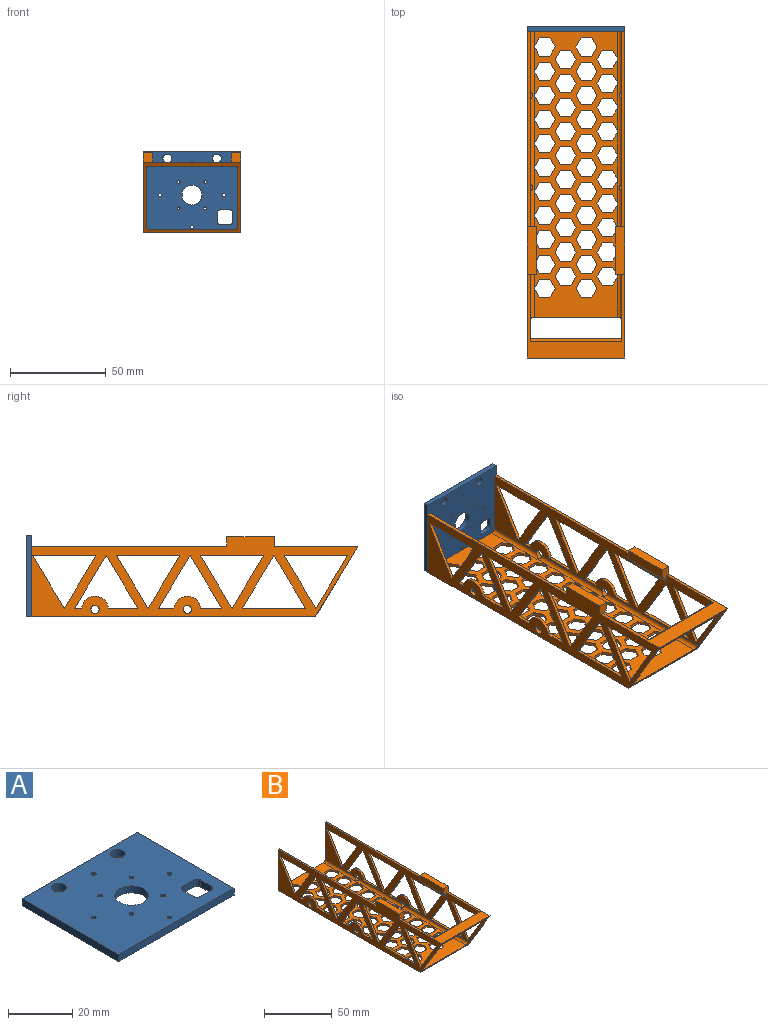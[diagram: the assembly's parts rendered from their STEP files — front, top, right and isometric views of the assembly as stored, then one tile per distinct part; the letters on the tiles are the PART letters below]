
ASSEMBLY  parts=2 mates=1
PART A: 25 faces, bbox 50.8x42.8x2.7 mm
  f0: cylinder r=1.5mm len=2.66mm, axis (0,0,-1), area 6.3mm2, adj f1,f20,f23,f24
  f1: plane 4.72x2.66mm, normal (-1,0,0), area 12.6mm2, adj f0,f2,f23,f24
  f2: cylinder r=1.5mm len=2.66mm, axis (0,0,-1), area 6.3mm2, adj f1,f3,f23,f24
  f3: plane 4.9x2.66mm, normal (0,1,0), area 13mm2, adj f2,f4,f23,f24
  f4: cylinder r=1.5mm len=2.66mm, axis (0,0,-1), area 6.3mm2, adj f3,f5,f23,f24
  f5: plane 4.72x2.66mm, normal (1,0,0), area 12.6mm2, adj f4,f6,f23,f24
  f6: cylinder r=1.5mm len=2.66mm, axis (0,0,-1), area 6.3mm2, adj f5,f20,f23,f24
  f7: plane 42.8x2.66mm, normal (1,0,0), area 113.8mm2, adj f8,f21,f23,f24
  f8: plane 50.75x2.66mm, normal (0,1,0), area 135mm2, adj f7,f9,f23,f24
  f9: plane 42.8x2.66mm, normal (-1,0,0), area 113.8mm2, adj f8,f21,f23,f24
  f10: cylinder r=0.75mm len=2.66mm, axis (0,0,-1), area 12.5mm2, adj f23,f24
  f11: cylinder r=0.75mm len=2.66mm, axis (0,0,-1), area 12.5mm2, adj f23,f24
  f12: cylinder r=0.75mm len=2.66mm, axis (0,0,-1), area 12.5mm2, adj f23,f24
  f13: cylinder r=0.75mm len=2.66mm, axis (0,0,-1), area 12.5mm2, adj f23,f24
  f14: cylinder r=0.75mm len=2.66mm, axis (0,0,-1), area 12.5mm2, adj f23,f24
  f15: cylinder r=0.75mm len=2.66mm, axis (0,0,-1), area 12.5mm2, adj f23,f24
  f16: cylinder r=0.75mm len=2.66mm, axis (0,0,-1), area 12.5mm2, adj f23,f24
  f17: cylinder r=2.3mm len=4.6mm, axis (0,0,-1), area 38.4mm2, adj f23,f24
  f18: cylinder r=2.3mm len=4.6mm, axis (0,0,-1), area 38.4mm2, adj f23,f24
  f19: cylinder r=5.22mm len=10.44mm, axis (0,0,-1), area 87.2mm2, adj f23,f24
  f20: plane 4.9x2.66mm, normal (0,-1,0), area 13mm2, adj f0,f6,f23,f24
  f21: plane 50.75x2.66mm, normal (0,-1,0), area 135mm2, adj f7,f9,f23,f24
  f22: cylinder r=0.75mm len=2.66mm, axis (0,0,-1), area 12.5mm2, adj f23,f24
  f23: plane 50.75x42.8mm, normal (0,0,1), area 1980.1mm2, adj f0,f1,f2,f3,f4,f5,f6,f7
  f24: plane 50.75x42.8mm, normal (0,0,-1), area 1980.1mm2, adj f0,f1,f2,f3,f4,f5,f6,f7
PART B: 341 faces, bbox 50.8x170.8x42 mm
  f0: plane 148.45x50.75mm, normal (0,0,-1), area 4287mm2, adj f4,f5,f14,f78,f79,f80,f81,f82
  f1: plane 149.4x43.59mm, normal (0,0,1), area 3265.6mm2, adj f6,f7,f14,f78,f79,f80,f81,f82
  f2: plane 169.25x33.42mm, normal (-1,0,0), area 2176.3mm2, adj f6,f8,f9,f14,f15,f16,f18,f21
  f3: plane 169.25x33.42mm, normal (1,0,0), area 2176.3mm2, adj f7,f8,f9,f11,f12,f13,f14,f19
  f4: plane 170.76x42mm, normal (1,0,0), area 2961.7mm2, adj f0,f8,f10,f14,f15,f16,f18,f21
  f5: plane 170.76x42mm, normal (-1,0,0), area 2961.7mm2, adj f0,f8,f11,f12,f13,f14,f17,f19
  f6: cylinder r=2mm len=150.61mm, axis (0,-1,0), area 456.7mm2, adj f1,f2,f14,f21,f22,f92,f123,f136
  f7: cylinder r=2mm len=150.61mm, axis (0,-1,0), area 456.7mm2, adj f1,f3,f14,f19,f20,f340
  f8: plane 50.75x43.72mm, normal (0,0,1), area 559.1mm2, adj f2,f3,f4,f5,f13,f18,f77,f340
  f9: plane 47.59x7.34mm, normal (0,0,-1), area 349.2mm2, adj f2,f3,f77,f340
  f10: plane 24.8x4.75mm, normal (0,0,1), area 117.8mm2, adj f4,f16,f18,f74
  f11: plane 102.24x1.58mm, normal (0,0,1), area 161.5mm2, adj f3,f5,f12,f14
  f12: plane 9.65x4.75mm, normal (0,1,0), area 27.8mm2, adj f3,f5,f11,f17,f73,f76
  f13: plane 9.65x4.75mm, normal (0,-1,0), area 27.8mm2, adj f3,f5,f8,f17,f73,f76
  f14: plane 50.75x37mm, normal (0,1,0), area 193.8mm2, adj f0,f1,f2,f3,f4,f5,f6,f7
  f15: plane 102.24x1.58mm, normal (0,0,1), area 161.5mm2, adj f2,f4,f14,f16
  f16: plane 9.65x4.75mm, normal (0,1,0), area 27.8mm2, adj f2,f4,f10,f15,f74,f75
  f17: plane 24.8x4.75mm, normal (0,0,1), area 117.8mm2, adj f5,f12,f13,f73
  f18: plane 9.65x4.75mm, normal (0,-1,0), area 27.8mm2, adj f2,f4,f8,f10,f74,f75
  f19: cylinder r=2.15mm len=4.3mm, axis (-1,0,0), area 24.8mm2, adj f3,f5,f7
  f20: cylinder r=2.15mm len=4.3mm, axis (-1,0,0), area 24.8mm2, adj f3,f5,f7
  f21: cylinder r=2.15mm len=4.3mm, axis (-1,0,0), area 24.8mm2, adj f2,f4,f6
  f22: cylinder r=2.15mm len=4.3mm, axis (-1,0,0), area 24.8mm2, adj f2,f4,f6
  f23: plane 27.42x16.53mm, normal (0,-0.86,0.52), area 50.6mm2, adj f2,f4,f24,f25
  f24: plane 27.42x16.53mm, normal (0,0.86,0.52), area 50.6mm2, adj f2,f4,f23,f25
  f25: plane 33.06x1.58mm, normal (0,0,-1), area 52.2mm2, adj f2,f4,f23,f24
  f26: plane 27.42x16.53mm, normal (0,-0.86,0.52), area 50.6mm2, adj f2,f4,f27,f28
  f27: plane 27.42x16.53mm, normal (0,0.86,0.52), area 50.6mm2, adj f2,f4,f26,f28
  f28: plane 33.06x1.58mm, normal (0,0,-1), area 52.2mm2, adj f2,f4,f26,f27
  f29: plane 11.02x1.58mm, normal (0,0,1), area 17.4mm2, adj f2,f4,f30,f33
  f30: plane 27.42x16.53mm, normal (0,0.86,-0.52), area 50.6mm2, adj f2,f4,f29,f31
  f31: plane 27.42x16.53mm, normal (0,-0.86,-0.52), area 50.6mm2, adj f2,f4,f30,f32
  f32: plane 8.11x1.58mm, normal (0,0,1), area 12.8mm2, adj f2,f4,f31,f33
  f33: cylinder r=7mm len=13.93mm, axis (-1,0,0), area 32.5mm2, adj f2,f4,f29,f32
  f34: plane 27.42x16.53mm, normal (0,0.86,-0.52), area 50.6mm2, adj f2,f4,f35,f38
  f35: plane 27.42x16.53mm, normal (0,-0.86,-0.52), area 50.6mm2, adj f2,f4,f34,f36
  f36: plane 3.72x1.58mm, normal (0,0,1), area 5.9mm2, adj f2,f4,f35,f37
  f37: cylinder r=7mm len=13.93mm, axis (-1,0,0), area 32.5mm2, adj f2,f4,f36,f38
  f38: plane 15.41x1.58mm, normal (0,0,1), area 24.4mm2, adj f2,f4,f34,f37
  f39: plane 33.06x1.58mm, normal (0,0,1), area 52.2mm2, adj f2,f4,f40,f41
  f40: plane 27.42x16.53mm, normal (0,0.86,-0.52), area 50.6mm2, adj f2,f4,f39,f41
  f41: plane 27.42x16.53mm, normal (0,-0.86,-0.52), area 50.6mm2, adj f2,f4,f39,f40
  f42: plane 27.42x16.53mm, normal (0,-0.86,0.52), area 50.6mm2, adj f2,f4,f43,f44
  f43: plane 27.42x16.53mm, normal (0,0.86,0.52), area 50.6mm2, adj f2,f4,f42,f44
  f44: plane 33.06x1.58mm, normal (0,0,-1), area 52.2mm2, adj f2,f4,f42,f43
  f45: plane 27.42x16.53mm, normal (0,-0.86,0.52), area 50.6mm2, adj f2,f4,f46,f47
  f46: plane 27.42x16.53mm, normal (0,0.86,0.52), area 50.6mm2, adj f2,f4,f45,f47
  f47: plane 33.06x1.58mm, normal (0,0,-1), area 52.2mm2, adj f2,f4,f45,f46
  f48: plane 33.06x1.58mm, normal (0,0,-1), area 52.2mm2, adj f3,f5,f49,f50
  f49: plane 27.42x16.53mm, normal (0,0.86,0.52), area 50.6mm2, adj f3,f5,f48,f50
  f50: plane 27.42x16.53mm, normal (0,-0.86,0.52), area 50.6mm2, adj f3,f5,f48,f49
  f51: plane 33.06x1.58mm, normal (0,0,-1), area 52.2mm2, adj f3,f5,f52,f53
  f52: plane 27.42x16.53mm, normal (0,0.86,0.52), area 50.6mm2, adj f3,f5,f51,f53
  f53: plane 27.42x16.53mm, normal (0,-0.86,0.52), area 50.6mm2, adj f3,f5,f51,f52
  f54: cylinder r=7mm len=13.93mm, axis (-1,0,0), area 32.5mm2, adj f3,f5,f55,f58
  f55: plane 8.11x1.58mm, normal (0,0,1), area 12.8mm2, adj f3,f5,f54,f56
  f56: plane 27.42x16.53mm, normal (0,-0.86,-0.52), area 50.6mm2, adj f3,f5,f55,f57
  f57: plane 27.42x16.53mm, normal (0,0.86,-0.52), area 50.6mm2, adj f3,f5,f56,f58
  f58: plane 11.02x1.58mm, normal (0,0,1), area 17.4mm2, adj f3,f5,f54,f57
  f59: plane 15.41x1.58mm, normal (0,0,1), area 24.4mm2, adj f3,f5,f60,f63
  f60: cylinder r=7mm len=13.93mm, axis (-1,0,0), area 32.5mm2, adj f3,f5,f59,f61
  f61: plane 3.72x1.58mm, normal (0,0,1), area 5.9mm2, adj f3,f5,f60,f62
  f62: plane 27.42x16.53mm, normal (0,-0.86,-0.52), area 50.6mm2, adj f3,f5,f61,f63
  f63: plane 27.42x16.53mm, normal (0,0.86,-0.52), area 50.6mm2, adj f3,f5,f59,f62
  f64: plane 27.42x16.53mm, normal (0,-0.86,-0.52), area 50.6mm2, adj f3,f5,f65,f66
  f65: plane 27.42x16.53mm, normal (0,0.86,-0.52), area 50.6mm2, adj f3,f5,f64,f66
  f66: plane 33.06x1.58mm, normal (0,0,1), area 52.2mm2, adj f3,f5,f64,f65
  f67: plane 33.06x1.58mm, normal (0,0,-1), area 52.2mm2, adj f3,f5,f68,f69
  f68: plane 27.42x16.53mm, normal (0,0.86,0.52), area 50.6mm2, adj f3,f5,f67,f69
  f69: plane 27.42x16.53mm, normal (0,-0.86,0.52), area 50.6mm2, adj f3,f5,f67,f68
  f70: plane 33.06x1.58mm, normal (0,0,-1), area 52.2mm2, adj f3,f5,f71,f72
  f71: plane 27.42x16.53mm, normal (0,0.86,0.52), area 50.6mm2, adj f3,f5,f70,f72
  f72: plane 27.42x16.53mm, normal (0,-0.86,0.52), area 50.6mm2, adj f3,f5,f70,f71
  f73: plane 24.8x5mm, normal (1,0,0), area 124mm2, adj f12,f13,f17,f76
  f74: plane 24.8x5mm, normal (-1,0,0), area 124mm2, adj f10,f16,f18,f75
  f75: cylinder r=5mm len=24.8mm, axis (0,-1,0), area 148.3mm2, adj f2,f16,f18,f74
  f76: cylinder r=5mm len=24.8mm, axis (0,1,0), area 148.3mm2, adj f3,f12,f13,f73
  f77: cylinder r=1.25mm len=47.59mm, axis (1,0,0), area 186.9mm2, adj f2,f3,f8,f9
  f78: plane 4.72x2.73mm, normal (0.87,-0.5,0), area 8.6mm2, adj f0,f1,f79,f82
  f79: plane 4.72x2.73mm, normal (0.87,0.5,0), area 8.6mm2, adj f0,f1,f78,f83
  f80: plane 4.72x2.73mm, normal (-0.87,0.5,0), area 8.6mm2, adj f0,f1,f81,f83
  f81: plane 4.72x2.73mm, normal (-0.87,-0.5,0), area 8.6mm2, adj f0,f1,f80,f82
  f82: plane 5.46x1.58mm, normal (0,-1,0), area 8.6mm2, adj f0,f1,f78,f81
  f83: plane 5.46x1.58mm, normal (0,1,0), area 8.6mm2, adj f0,f1,f79,f80
  f84: plane 4.72x2.73mm, normal (0.87,-0.5,0), area 8.6mm2, adj f0,f1,f85,f89
  f85: plane 4.72x2.73mm, normal (0.87,0.5,0), area 8.6mm2, adj f0,f1,f84,f86
  f86: plane 5.46x1.58mm, normal (0,1,0), area 8.6mm2, adj f0,f1,f85,f87
  f87: plane 4.72x2.73mm, normal (-0.87,0.5,0), area 8.6mm2, adj f0,f1,f86,f88
  f88: plane 4.72x2.73mm, normal (-0.87,-0.5,0), area 8.6mm2, adj f0,f1,f87,f89
  f89: plane 5.46x1.58mm, normal (0,-1,0), area 8.6mm2, adj f0,f1,f84,f88
  f90: plane 4.63x2.67mm, normal (-0.87,-0.5,0), area 8.4mm2, adj f0,f1,f92,f93
  f91: plane 4.63x2.67mm, normal (-0.87,0.5,0), area 8.4mm2, adj f0,f1,f92,f96
  f92: plane 1.58x0.19mm, normal (-1,0,0), area 0.3mm2, adj f0,f6,f90,f91
  f93: plane 5.46x1.58mm, normal (0,-1,0), area 8.6mm2, adj f0,f1,f90,f94
  f94: plane 4.72x2.73mm, normal (0.87,-0.5,0), area 8.6mm2, adj f0,f1,f93,f95
  f95: plane 4.72x2.73mm, normal (0.87,0.5,0), area 8.6mm2, adj f0,f1,f94,f96
  f96: plane 5.46x1.58mm, normal (0,1,0), area 8.6mm2, adj f0,f1,f91,f95
  f97: plane 5.46x1.58mm, normal (0,1,0), area 8.6mm2, adj f0,f1,f98,f102
  f98: plane 4.72x2.73mm, normal (-0.87,0.5,0), area 8.6mm2, adj f0,f1,f97,f99
  f99: plane 4.72x2.73mm, normal (-0.87,-0.5,0), area 8.6mm2, adj f0,f1,f98,f100
  f100: plane 5.46x1.58mm, normal (0,-1,0), area 8.6mm2, adj f0,f1,f99,f101
  f101: plane 4.72x2.73mm, normal (0.87,-0.5,0), area 8.6mm2, adj f0,f1,f100,f102
  f102: plane 4.72x2.73mm, normal (0.87,0.5,0), area 8.6mm2, adj f0,f1,f97,f101
  f103: plane 4.72x2.73mm, normal (-0.87,0.5,0), area 8.6mm2, adj f0,f1,f104,f108
  f104: plane 4.72x2.73mm, normal (-0.87,-0.5,0), area 8.6mm2, adj f0,f1,f103,f105
  f105: plane 5.46x1.58mm, normal (0,-1,0), area 8.6mm2, adj f0,f1,f104,f106
  f106: plane 4.72x2.73mm, normal (0.87,-0.5,0), area 8.6mm2, adj f0,f1,f105,f107
  f107: plane 4.72x2.73mm, normal (0.87,0.5,0), area 8.6mm2, adj f0,f1,f106,f108
  f108: plane 5.46x1.58mm, normal (0,1,0), area 8.6mm2, adj f0,f1,f103,f107
  f109: plane 4.72x2.73mm, normal (-0.87,0.5,0), area 8.6mm2, adj f0,f1,f110,f114
  f110: plane 4.72x2.73mm, normal (-0.87,-0.5,0), area 8.6mm2, adj f0,f1,f109,f111
  f111: plane 5.46x1.58mm, normal (0,-1,0), area 8.6mm2, adj f0,f1,f110,f112
  f112: plane 4.72x2.73mm, normal (0.87,-0.5,0), area 8.6mm2, adj f0,f1,f111,f113
  f113: plane 4.72x2.73mm, normal (0.87,0.5,0), area 8.6mm2, adj f0,f1,f112,f114
  f114: plane 5.46x1.58mm, normal (0,1,0), area 8.6mm2, adj f0,f1,f109,f113
  f115: plane 5.46x1.58mm, normal (0,1,0), area 8.6mm2, adj f0,f1,f116,f120
  f116: plane 4.72x2.73mm, normal (-0.87,0.5,0), area 8.6mm2, adj f0,f1,f115,f117
  f117: plane 4.72x2.73mm, normal (-0.87,-0.5,0), area 8.6mm2, adj f0,f1,f116,f118
  f118: plane 5.46x1.58mm, normal (0,-1,0), area 8.6mm2, adj f0,f1,f117,f119
  f119: plane 4.72x2.73mm, normal (0.87,-0.5,0), area 8.6mm2, adj f0,f1,f118,f120
  f120: plane 4.72x2.73mm, normal (0.87,0.5,0), area 8.6mm2, adj f0,f1,f115,f119
  f121: plane 4.63x2.68mm, normal (-0.87,-0.5,0), area 8.5mm2, adj f0,f1,f123,f124
  f122: plane 4.63x2.68mm, normal (-0.87,0.5,0), area 8.5mm2, adj f0,f1,f123,f127
  f123: plane 1.58x0.18mm, normal (-1,0,0), area 0.3mm2, adj f0,f6,f121,f122
  f124: plane 5.46x1.58mm, normal (0,-1,0), area 8.6mm2, adj f0,f1,f121,f125
  f125: plane 4.72x2.73mm, normal (0.87,-0.5,0), area 8.6mm2, adj f0,f1,f124,f126
  f126: plane 4.72x2.73mm, normal (0.87,0.5,0), area 8.6mm2, adj f0,f1,f125,f127
  f127: plane 5.46x1.58mm, normal (0,1,0), area 8.6mm2, adj f0,f1,f122,f126
  f128: plane 4.72x2.73mm, normal (0.87,-0.5,0), area 8.6mm2, adj f0,f1,f129,f133
  f129: plane 4.72x2.73mm, normal (0.87,0.5,0), area 8.6mm2, adj f0,f1,f128,f130
  f130: plane 5.46x1.58mm, normal (0,1,0), area 8.6mm2, adj f0,f1,f129,f131
  f131: plane 4.72x2.73mm, normal (-0.87,0.5,0), area 8.6mm2, adj f0,f1,f130,f132
  f132: plane 4.72x2.73mm, normal (-0.87,-0.5,0), area 8.6mm2, adj f0,f1,f131,f133
  f133: plane 5.46x1.58mm, normal (0,-1,0), area 8.6mm2, adj f0,f1,f128,f132
  f134: plane 4.63x2.67mm, normal (-0.87,-0.5,0), area 8.4mm2, adj f0,f1,f136,f137
  f135: plane 4.63x2.67mm, normal (-0.87,0.5,0), area 8.4mm2, adj f0,f1,f136,f140
  f136: plane 1.58x0.2mm, normal (-1,0,0), area 0.3mm2, adj f0,f6,f134,f135
  f137: plane 5.46x1.58mm, normal (0,-1,0), area 8.6mm2, adj f0,f1,f134,f138
  f138: plane 4.72x2.73mm, normal (0.87,-0.5,0), area 8.6mm2, adj f0,f1,f137,f139
  f139: plane 4.72x2.73mm, normal (0.87,0.5,0), area 8.6mm2, adj f0,f1,f138,f140
  f140: plane 5.46x1.58mm, normal (0,1,0), area 8.6mm2, adj f0,f1,f135,f139
  f141: plane 4.72x2.73mm, normal (0.87,-0.5,0), area 8.6mm2, adj f0,f1,f142,f146
  f142: plane 4.72x2.73mm, normal (0.87,0.5,0), area 8.6mm2, adj f0,f1,f141,f143
  f143: plane 5.46x1.58mm, normal (0,1,0), area 8.6mm2, adj f0,f1,f142,f144
  f144: plane 4.72x2.73mm, normal (-0.87,0.5,0), area 8.6mm2, adj f0,f1,f143,f145
  f145: plane 4.72x2.73mm, normal (-0.87,-0.5,0), area 8.6mm2, adj f0,f1,f144,f146
  f146: plane 5.46x1.58mm, normal (0,-1,0), area 8.6mm2, adj f0,f1,f141,f145
  f147: plane 4.62x2.67mm, normal (-0.87,-0.5,0), area 8.4mm2, adj f0,f1,f149,f150
  f148: plane 4.62x2.67mm, normal (-0.87,0.5,0), area 8.4mm2, adj f0,f1,f149,f153
  f149: plane 1.58x0.21mm, normal (-1,0,0), area 0.3mm2, adj f0,f6,f147,f148
  f150: plane 5.46x1.58mm, normal (0,-1,0), area 8.6mm2, adj f0,f1,f147,f151
  f151: plane 4.72x2.73mm, normal (0.87,-0.5,0), area 8.6mm2, adj f0,f1,f150,f152
  f152: plane 4.72x2.73mm, normal (0.87,0.5,0), area 8.6mm2, adj f0,f1,f151,f153
  f153: plane 5.46x1.58mm, normal (0,1,0), area 8.6mm2, adj f0,f1,f148,f152
  f154: plane 4.62x2.67mm, normal (-0.87,-0.5,0), area 8.4mm2, adj f0,f1,f156,f157
  f155: plane 4.62x2.67mm, normal (-0.87,0.5,0), area 8.4mm2, adj f0,f1,f156,f160
  f156: plane 1.58x0.22mm, normal (-1,0,0), area 0.3mm2, adj f0,f6,f154,f155
  f157: plane 5.46x1.58mm, normal (0,-1,0), area 8.6mm2, adj f0,f1,f154,f158
  f158: plane 4.72x2.73mm, normal (0.87,-0.5,0), area 8.6mm2, adj f0,f1,f157,f159
  f159: plane 4.72x2.73mm, normal (0.87,0.5,0), area 8.6mm2, adj f0,f1,f158,f160
  f160: plane 5.46x1.58mm, normal (0,1,0), area 8.6mm2, adj f0,f1,f155,f159
  f161: plane 4.72x2.73mm, normal (-0.87,0.5,0), area 8.6mm2, adj f0,f1,f162,f166
  f162: plane 4.72x2.73mm, normal (-0.87,-0.5,0), area 8.6mm2, adj f0,f1,f161,f163
  f163: plane 5.46x1.58mm, normal (0,-1,0), area 8.6mm2, adj f0,f1,f162,f164
  f164: plane 4.72x2.73mm, normal (0.87,-0.5,0), area 8.6mm2, adj f0,f1,f163,f165
  f165: plane 4.72x2.73mm, normal (0.87,0.5,0), area 8.6mm2, adj f0,f1,f164,f166
  f166: plane 5.46x1.58mm, normal (0,1,0), area 8.6mm2, adj f0,f1,f161,f165
  f167: plane 5.46x1.58mm, normal (0,1,0), area 8.6mm2, adj f0,f1,f168,f172
  f168: plane 4.72x2.73mm, normal (-0.87,0.5,0), area 8.6mm2, adj f0,f1,f167,f169
  f169: plane 4.72x2.73mm, normal (-0.87,-0.5,0), area 8.6mm2, adj f0,f1,f168,f170
  f170: plane 5.46x1.58mm, normal (0,-1,0), area 8.6mm2, adj f0,f1,f169,f171
  f171: plane 4.72x2.73mm, normal (0.87,-0.5,0), area 8.6mm2, adj f0,f1,f170,f172
  f172: plane 4.72x2.73mm, normal (0.87,0.5,0), area 8.6mm2, adj f0,f1,f167,f171
  f173: plane 4.72x2.73mm, normal (-0.87,0.5,0), area 8.6mm2, adj f0,f1,f174,f178
  f174: plane 4.72x2.73mm, normal (-0.87,-0.5,0), area 8.6mm2, adj f0,f1,f173,f175
  f175: plane 5.46x1.58mm, normal (0,-1,0), area 8.6mm2, adj f0,f1,f174,f176
  f176: plane 4.72x2.73mm, normal (0.87,-0.5,0), area 8.6mm2, adj f0,f1,f175,f177
  f177: plane 4.72x2.73mm, normal (0.87,0.5,0), area 8.6mm2, adj f0,f1,f176,f178
  f178: plane 5.46x1.58mm, normal (0,1,0), area 8.6mm2, adj f0,f1,f173,f177
  f179: plane 5.46x1.58mm, normal (0,1,0), area 8.6mm2, adj f0,f1,f180,f184
  f180: plane 4.72x2.73mm, normal (-0.87,0.5,0), area 8.6mm2, adj f0,f1,f179,f181
  f181: plane 4.72x2.73mm, normal (-0.87,-0.5,0), area 8.6mm2, adj f0,f1,f180,f182
  f182: plane 5.46x1.58mm, normal (0,-1,0), area 8.6mm2, adj f0,f1,f181,f183
  f183: plane 4.72x2.73mm, normal (0.87,-0.5,0), area 8.6mm2, adj f0,f1,f182,f184
  f184: plane 4.72x2.73mm, normal (0.87,0.5,0), area 8.6mm2, adj f0,f1,f179,f183
  f185: plane 5.46x1.58mm, normal (0,1,0), area 8.6mm2, adj f0,f1,f186,f190
  f186: plane 4.72x2.73mm, normal (-0.87,0.5,0), area 8.6mm2, adj f0,f1,f185,f187
  f187: plane 4.72x2.73mm, normal (-0.87,-0.5,0), area 8.6mm2, adj f0,f1,f186,f188
  f188: plane 5.46x1.58mm, normal (0,-1,0), area 8.6mm2, adj f0,f1,f187,f189
  f189: plane 4.72x2.73mm, normal (0.87,-0.5,0), area 8.6mm2, adj f0,f1,f188,f190
  f190: plane 4.72x2.73mm, normal (0.87,0.5,0), area 8.6mm2, adj f0,f1,f185,f189
  f191: plane 5.46x1.58mm, normal (0,1,0), area 8.6mm2, adj f0,f1,f192,f196
  f192: plane 4.72x2.73mm, normal (-0.87,0.5,0), area 8.6mm2, adj f0,f1,f191,f193
  f193: plane 4.72x2.73mm, normal (-0.87,-0.5,0), area 8.6mm2, adj f0,f1,f192,f194
  f194: plane 5.46x1.58mm, normal (0,-1,0), area 8.6mm2, adj f0,f1,f193,f195
  f195: plane 4.72x2.73mm, normal (0.87,-0.5,0), area 8.6mm2, adj f0,f1,f194,f196
  f196: plane 4.72x2.73mm, normal (0.87,0.5,0), area 8.6mm2, adj f0,f1,f191,f195
  f197: plane 4.72x2.73mm, normal (0.87,-0.5,0), area 8.6mm2, adj f0,f1,f198,f202
  f198: plane 4.72x2.73mm, normal (0.87,0.5,0), area 8.6mm2, adj f0,f1,f197,f199
  f199: plane 5.46x1.58mm, normal (0,1,0), area 8.6mm2, adj f0,f1,f198,f200
  f200: plane 4.72x2.73mm, normal (-0.87,0.5,0), area 8.6mm2, adj f0,f1,f199,f201
  f201: plane 4.72x2.73mm, normal (-0.87,-0.5,0), area 8.6mm2, adj f0,f1,f200,f202
  f202: plane 5.46x1.58mm, normal (0,-1,0), area 8.6mm2, adj f0,f1,f197,f201
  f203: plane 4.72x2.73mm, normal (-0.87,0.5,0), area 8.6mm2, adj f0,f1,f204,f208
  f204: plane 4.72x2.73mm, normal (-0.87,-0.5,0), area 8.6mm2, adj f0,f1,f203,f205
  f205: plane 5.46x1.58mm, normal (0,-1,0), area 8.6mm2, adj f0,f1,f204,f206
  f206: plane 4.72x2.73mm, normal (0.87,-0.5,0), area 8.6mm2, adj f0,f1,f205,f207
  f207: plane 4.72x2.73mm, normal (0.87,0.5,0), area 8.6mm2, adj f0,f1,f206,f208
  f208: plane 5.46x1.58mm, normal (0,1,0), area 8.6mm2, adj f0,f1,f203,f207
  f209: plane 5.46x1.58mm, normal (0,-1,0), area 8.6mm2, adj f0,f1,f210,f214
  f210: plane 4.72x2.73mm, normal (0.87,-0.5,0), area 8.6mm2, adj f0,f1,f209,f211
  f211: plane 4.72x2.73mm, normal (0.87,0.5,0), area 8.6mm2, adj f0,f1,f210,f212
  f212: plane 5.46x1.58mm, normal (0,1,0), area 8.6mm2, adj f0,f1,f211,f213
  f213: plane 4.72x2.73mm, normal (-0.87,0.5,0), area 8.6mm2, adj f0,f1,f212,f214
  f214: plane 4.72x2.73mm, normal (-0.87,-0.5,0), area 8.6mm2, adj f0,f1,f209,f213
  f215: plane 5.46x1.58mm, normal (0,1,0), area 8.6mm2, adj f0,f1,f216,f220
  f216: plane 4.72x2.73mm, normal (-0.87,0.5,0), area 8.6mm2, adj f0,f1,f215,f217
  f217: plane 4.72x2.73mm, normal (-0.87,-0.5,0), area 8.6mm2, adj f0,f1,f216,f218
  f218: plane 5.46x1.58mm, normal (0,-1,0), area 8.6mm2, adj f0,f1,f217,f219
  f219: plane 4.72x2.73mm, normal (0.87,-0.5,0), area 8.6mm2, adj f0,f1,f218,f220
  f220: plane 4.72x2.73mm, normal (0.87,0.5,0), area 8.6mm2, adj f0,f1,f215,f219
  f221: plane 4.69x2.71mm, normal (-0.87,-0.5,0), area 8.6mm2, adj f0,f1,f223,f224
  f222: plane 4.69x2.71mm, normal (-0.87,0.5,0), area 8.6mm2, adj f0,f1,f223,f227
  f223: plane 1.58x0.07mm, normal (-1,0,0), area 0.1mm2, adj f0,f6,f221,f222
  f224: plane 5.46x1.58mm, normal (0,-1,0), area 8.6mm2, adj f0,f1,f221,f225
  f225: plane 4.72x2.73mm, normal (0.87,-0.5,0), area 8.6mm2, adj f0,f1,f224,f226
  f226: plane 4.72x2.73mm, normal (0.87,0.5,0), area 8.6mm2, adj f0,f1,f225,f227
  f227: plane 5.46x1.58mm, normal (0,1,0), area 8.6mm2, adj f0,f1,f222,f226
  f228: plane 4.72x2.73mm, normal (-0.87,0.5,0), area 8.6mm2, adj f0,f1,f229,f233
  f229: plane 4.72x2.73mm, normal (-0.87,-0.5,0), area 8.6mm2, adj f0,f1,f228,f230
  f230: plane 5.46x1.58mm, normal (0,-1,0), area 8.6mm2, adj f0,f1,f229,f231
  f231: plane 4.72x2.73mm, normal (0.87,-0.5,0), area 8.6mm2, adj f0,f1,f230,f232
  f232: plane 4.72x2.73mm, normal (0.87,0.5,0), area 8.6mm2, adj f0,f1,f231,f233
  f233: plane 5.46x1.58mm, normal (0,1,0), area 8.6mm2, adj f0,f1,f228,f232
  f234: plane 4.72x2.73mm, normal (0.87,-0.5,0), area 8.6mm2, adj f0,f1,f235,f239
  f235: plane 4.72x2.73mm, normal (0.87,0.5,0), area 8.6mm2, adj f0,f1,f234,f236
  f236: plane 5.46x1.58mm, normal (0,1,0), area 8.6mm2, adj f0,f1,f235,f237
  f237: plane 4.72x2.73mm, normal (-0.87,0.5,0), area 8.6mm2, adj f0,f1,f236,f238
  f238: plane 4.72x2.73mm, normal (-0.87,-0.5,0), area 8.6mm2, adj f0,f1,f237,f239
  f239: plane 5.46x1.58mm, normal (0,-1,0), area 8.6mm2, adj f0,f1,f234,f238
  f240: plane 4.64x2.68mm, normal (-0.87,-0.5,0), area 8.5mm2, adj f0,f1,f242,f243
  f241: plane 4.64x2.68mm, normal (-0.87,0.5,0), area 8.5mm2, adj f0,f1,f242,f246
  f242: plane 1.58x0.17mm, normal (-1,0,0), area 0.3mm2, adj f0,f6,f240,f241
  f243: plane 5.46x1.58mm, normal (0,-1,0), area 8.6mm2, adj f0,f1,f240,f244
  f244: plane 4.72x2.73mm, normal (0.87,-0.5,0), area 8.6mm2, adj f0,f1,f243,f245
  f245: plane 4.72x2.73mm, normal (0.87,0.5,0), area 8.6mm2, adj f0,f1,f244,f246
  f246: plane 5.46x1.58mm, normal (0,1,0), area 8.6mm2, adj f0,f1,f241,f245
  f247: plane 5.46x1.58mm, normal (0,1,0), area 8.6mm2, adj f0,f1,f248,f252
  f248: plane 4.72x2.73mm, normal (-0.87,0.5,0), area 8.6mm2, adj f0,f1,f247,f249
  f249: plane 4.72x2.73mm, normal (-0.87,-0.5,0), area 8.6mm2, adj f0,f1,f248,f250
  f250: plane 5.46x1.58mm, normal (0,-1,0), area 8.6mm2, adj f0,f1,f249,f251
  f251: plane 4.72x2.73mm, normal (0.87,-0.5,0), area 8.6mm2, adj f0,f1,f250,f252
  f252: plane 4.72x2.73mm, normal (0.87,0.5,0), area 8.6mm2, adj f0,f1,f247,f251
  f253: plane 4.72x2.73mm, normal (-0.87,0.5,0), area 8.6mm2, adj f0,f1,f254,f258
  f254: plane 4.72x2.73mm, normal (-0.87,-0.5,0), area 8.6mm2, adj f0,f1,f253,f255
  f255: plane 5.46x1.58mm, normal (0,-1,0), area 8.6mm2, adj f0,f1,f254,f256
  f256: plane 4.72x2.73mm, normal (0.87,-0.5,0), area 8.6mm2, adj f0,f1,f255,f257
  f257: plane 4.72x2.73mm, normal (0.87,0.5,0), area 8.6mm2, adj f0,f1,f256,f258
  f258: plane 5.46x1.58mm, normal (0,1,0), area 8.6mm2, adj f0,f1,f253,f257
  f259: plane 4.64x2.68mm, normal (-0.87,-0.5,0), area 8.5mm2, adj f0,f1,f261,f262
  f260: plane 4.64x2.68mm, normal (-0.87,0.5,0), area 8.5mm2, adj f0,f1,f261,f265
  f261: plane 1.58x0.16mm, normal (-1,0,0), area 0.3mm2, adj f0,f6,f259,f260
  f262: plane 5.46x1.58mm, normal (0,-1,0), area 8.6mm2, adj f0,f1,f259,f263
  f263: plane 4.72x2.73mm, normal (0.87,-0.5,0), area 8.6mm2, adj f0,f1,f262,f264
  f264: plane 4.72x2.73mm, normal (0.87,0.5,0), area 8.6mm2, adj f0,f1,f263,f265
  f265: plane 5.46x1.58mm, normal (0,1,0), area 8.6mm2, adj f0,f1,f260,f264
  f266: plane 4.72x2.73mm, normal (0.87,-0.5,0), area 8.6mm2, adj f0,f1,f267,f271
  f267: plane 4.72x2.73mm, normal (0.87,0.5,0), area 8.6mm2, adj f0,f1,f266,f268
  f268: plane 5.46x1.58mm, normal (0,1,0), area 8.6mm2, adj f0,f1,f267,f269
  f269: plane 4.72x2.73mm, normal (-0.87,0.5,0), area 8.6mm2, adj f0,f1,f268,f270
  f270: plane 4.72x2.73mm, normal (-0.87,-0.5,0), area 8.6mm2, adj f0,f1,f269,f271
  f271: plane 5.46x1.58mm, normal (0,-1,0), area 8.6mm2, adj f0,f1,f266,f270
  f272: plane 4.65x2.68mm, normal (-0.87,0.5,0), area 8.5mm2, adj f0,f1,f273,f278
  f273: plane 1.58x0.15mm, normal (-1,0,0), area 0.2mm2, adj f0,f6,f272,f274
  f274: plane 4.65x2.68mm, normal (-0.87,-0.5,0), area 8.5mm2, adj f0,f1,f273,f275
  f275: plane 5.46x1.58mm, normal (0,-1,0), area 8.6mm2, adj f0,f1,f274,f276
  f276: plane 4.72x2.73mm, normal (0.87,-0.5,0), area 8.6mm2, adj f0,f1,f275,f277
  f277: plane 4.72x2.73mm, normal (0.87,0.5,0), area 8.6mm2, adj f0,f1,f276,f278
  f278: plane 5.46x1.58mm, normal (0,1,0), area 8.6mm2, adj f0,f1,f272,f277
  f279: plane 5.46x1.58mm, normal (0,1,0), area 8.6mm2, adj f0,f1,f280,f284
  f280: plane 4.72x2.73mm, normal (-0.87,0.5,0), area 8.6mm2, adj f0,f1,f279,f281
  f281: plane 4.72x2.73mm, normal (-0.87,-0.5,0), area 8.6mm2, adj f0,f1,f280,f282
  f282: plane 5.46x1.58mm, normal (0,-1,0), area 8.6mm2, adj f0,f1,f281,f283
  f283: plane 4.72x2.73mm, normal (0.87,-0.5,0), area 8.6mm2, adj f0,f1,f282,f284
  f284: plane 4.72x2.73mm, normal (0.87,0.5,0), area 8.6mm2, adj f0,f1,f279,f283
  f285: plane 4.72x2.73mm, normal (0.87,-0.5,0), area 8.6mm2, adj f0,f1,f286,f290
  f286: plane 4.72x2.73mm, normal (0.87,0.5,0), area 8.6mm2, adj f0,f1,f285,f287
  f287: plane 5.46x1.58mm, normal (0,1,0), area 8.6mm2, adj f0,f1,f286,f288
  f288: plane 4.72x2.73mm, normal (-0.87,0.5,0), area 8.6mm2, adj f0,f1,f287,f289
  f289: plane 4.72x2.73mm, normal (-0.87,-0.5,0), area 8.6mm2, adj f0,f1,f288,f290
  f290: plane 5.46x1.58mm, normal (0,-1,0), area 8.6mm2, adj f0,f1,f285,f289
  f291: plane 4.72x2.73mm, normal (-0.87,0.5,0), area 8.6mm2, adj f0,f1,f292,f296
  f292: plane 4.72x2.73mm, normal (-0.87,-0.5,0), area 8.6mm2, adj f0,f1,f291,f293
  f293: plane 5.46x1.58mm, normal (0,-1,0), area 8.6mm2, adj f0,f1,f292,f294
  f294: plane 4.72x2.73mm, normal (0.87,-0.5,0), area 8.6mm2, adj f0,f1,f293,f295
  f295: plane 4.72x2.73mm, normal (0.87,0.5,0), area 8.6mm2, adj f0,f1,f294,f296
  f296: plane 5.46x1.58mm, normal (0,1,0), area 8.6mm2, adj f0,f1,f291,f295
  f297: plane 4.72x2.73mm, normal (0.87,-0.5,0), area 8.6mm2, adj f0,f1,f298,f302
  f298: plane 4.72x2.73mm, normal (0.87,0.5,0), area 8.6mm2, adj f0,f1,f297,f299
  f299: plane 5.46x1.58mm, normal (0,1,0), area 8.6mm2, adj f0,f1,f298,f300
  f300: plane 4.72x2.73mm, normal (-0.87,0.5,0), area 8.6mm2, adj f0,f1,f299,f301
  f301: plane 4.72x2.73mm, normal (-0.87,-0.5,0), area 8.6mm2, adj f0,f1,f300,f302
  f302: plane 5.46x1.58mm, normal (0,-1,0), area 8.6mm2, adj f0,f1,f297,f301
  f303: plane 4.61x2.66mm, normal (-0.87,-0.5,0), area 8.4mm2, adj f0,f1,f305,f306
  f304: plane 4.61x2.66mm, normal (-0.87,0.5,0), area 8.4mm2, adj f0,f1,f305,f309
  f305: plane 1.58x0.23mm, normal (-1,0,0), area 0.4mm2, adj f0,f6,f303,f304
  f306: plane 5.46x1.58mm, normal (0,-1,0), area 8.6mm2, adj f0,f1,f303,f307
  f307: plane 4.72x2.73mm, normal (0.87,-0.5,0), area 8.6mm2, adj f0,f1,f306,f308
  f308: plane 4.72x2.73mm, normal (0.87,0.5,0), area 8.6mm2, adj f0,f1,f307,f309
  f309: plane 5.46x1.58mm, normal (0,1,0), area 8.6mm2, adj f0,f1,f304,f308
  f310: plane 4.72x2.73mm, normal (-0.87,0.5,0), area 8.6mm2, adj f0,f1,f311,f315
  f311: plane 4.72x2.73mm, normal (-0.87,-0.5,0), area 8.6mm2, adj f0,f1,f310,f312
  f312: plane 5.46x1.58mm, normal (0,-1,0), area 8.6mm2, adj f0,f1,f311,f313
  f313: plane 4.72x2.73mm, normal (0.87,-0.5,0), area 8.6mm2, adj f0,f1,f312,f314
  f314: plane 4.72x2.73mm, normal (0.87,0.5,0), area 8.6mm2, adj f0,f1,f313,f315
  f315: plane 5.46x1.58mm, normal (0,1,0), area 8.6mm2, adj f0,f1,f310,f314
  f316: plane 4.72x2.73mm, normal (0.87,-0.5,0), area 8.6mm2, adj f0,f1,f317,f321
  f317: plane 4.72x2.73mm, normal (0.87,0.5,0), area 8.6mm2, adj f0,f1,f316,f318
  f318: plane 5.46x1.58mm, normal (0,1,0), area 8.6mm2, adj f0,f1,f317,f319
  f319: plane 4.72x2.73mm, normal (-0.87,0.5,0), area 8.6mm2, adj f0,f1,f318,f320
  f320: plane 4.72x2.73mm, normal (-0.87,-0.5,0), area 8.6mm2, adj f0,f1,f319,f321
  f321: plane 5.46x1.58mm, normal (0,-1,0), area 8.6mm2, adj f0,f1,f316,f320
  f322: plane 5.46x1.58mm, normal (0,1,0), area 8.6mm2, adj f0,f1,f323,f327
  f323: plane 4.72x2.73mm, normal (-0.87,0.5,0), area 8.6mm2, adj f0,f1,f322,f324
  f324: plane 4.72x2.73mm, normal (-0.87,-0.5,0), area 8.6mm2, adj f0,f1,f323,f325
  f325: plane 5.46x1.58mm, normal (0,-1,0), area 8.6mm2, adj f0,f1,f324,f326
  f326: plane 4.72x2.73mm, normal (0.87,-0.5,0), area 8.6mm2, adj f0,f1,f325,f327
  f327: plane 4.72x2.73mm, normal (0.87,0.5,0), area 8.6mm2, adj f0,f1,f322,f326
  f328: plane 5.46x1.58mm, normal (0,1,0), area 8.6mm2, adj f0,f1,f329,f333
  f329: plane 4.72x2.73mm, normal (-0.87,0.5,0), area 8.6mm2, adj f0,f1,f328,f330
  f330: plane 4.72x2.73mm, normal (-0.87,-0.5,0), area 8.6mm2, adj f0,f1,f329,f331
  f331: plane 5.46x1.58mm, normal (0,-1,0), area 8.6mm2, adj f0,f1,f330,f332
  f332: plane 4.72x2.73mm, normal (0.87,-0.5,0), area 8.6mm2, adj f0,f1,f331,f333
  f333: plane 4.72x2.73mm, normal (0.87,0.5,0), area 8.6mm2, adj f0,f1,f328,f332
  f334: plane 5.46x1.58mm, normal (0,1,0), area 8.6mm2, adj f0,f1,f335,f339
  f335: plane 4.72x2.73mm, normal (-0.87,0.5,0), area 8.6mm2, adj f0,f1,f334,f336
  f336: plane 4.72x2.73mm, normal (-0.87,-0.5,0), area 8.6mm2, adj f0,f1,f335,f337
  f337: plane 5.46x1.58mm, normal (0,-1,0), area 8.6mm2, adj f0,f1,f336,f338
  f338: plane 4.72x2.73mm, normal (0.87,-0.5,0), area 8.6mm2, adj f0,f1,f337,f339
  f339: plane 4.72x2.73mm, normal (0.87,0.5,0), area 8.6mm2, adj f0,f1,f334,f338
  f340: plane 50.75x37mm, normal (0,-0.86,-0.52), area 365.3mm2, adj f0,f1,f2,f3,f4,f5,f6,f7
PLACE A rot(axis=(1,0,0),90deg) t=(16.12,108.27,-12.36)mm
PLACE B t=(-9.25,-4.07,-21.18)mm
MATE fastened B.f14 <-> A.f23  axis (0,1,0) through (16.12,105.61,-33.76)mm
